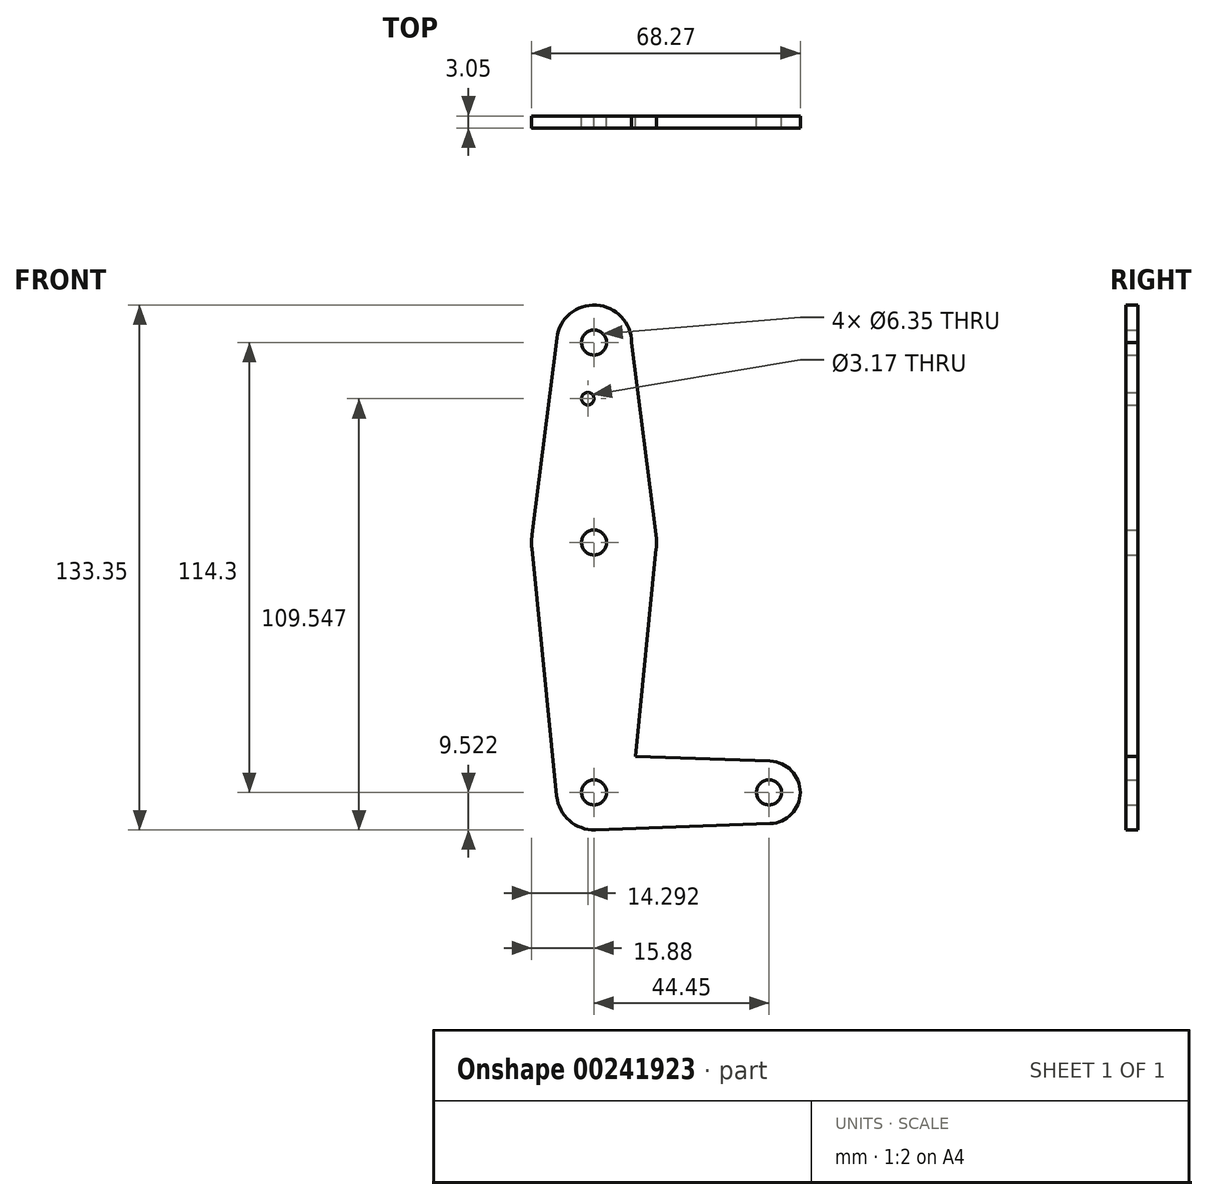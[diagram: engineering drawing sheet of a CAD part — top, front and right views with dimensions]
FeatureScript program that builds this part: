
annotation { "Feature Type Name" : "Feature", "Feature Type Description" : "" }
export const myFeature = defineFeature(function(context is Context, id is Id, definition is map)
    precondition{}
    {
        {
            var Q0;
            Q0=qCreatedBy(makeId("Front.planeOp"),FACE);
            var sketch = newSketch(context, id + "F0", { "sketchPlane" : qUnion([Q0])});
            skCircle(sketch, "E0", {"center": v(-0.34, 88.77) * mm, "radius": 9.53 * mm});
            skCircle(sketch, "E1", {"center": v(-0.34, 37.97) * mm, "radius": 15.88 * mm});
            skCircle(sketch, "E2", {"center": v(-0.34, -25.53) * mm, "radius": 9.53 * mm});
            skLineSegment(sketch, "E3", {"start": v(-0.34, 88.77) * mm, "end": v(-0.34, -25.53) * mm, "construction": true});
            skLineSegment(sketch, "E4", {"start": v(9.18, 88.77) * mm, "end": v(15.4, 39.98) * mm});
            skLineSegment(sketch, "E5", {"start": v(-9.8, 89.96) * mm, "end": v(-16.1, 39.96) * mm});
            skLineSegment(sketch, "E6", {"start": v(-9.82, -26.48) * mm, "end": v(-16.14, 36.38) * mm});
            skLineSegment(sketch, "E7", {"start": v(9.14, -26.48) * mm, "end": v(15.46, 36.38) * mm});
            skLineSegment(sketch, "E8", {"start": v(-0.34, -25.53) * mm, "end": v(44.1, -25.53) * mm, "construction": true});
            skCircle(sketch, "E9", {"center": v(44.1, -25.53) * mm, "radius": 7.94 * mm});
            skLineSegment(sketch, "E10", {"start": v(0, -16) * mm, "end": v(44.4, -17.6) * mm});
            skLineSegment(sketch, "E11", {"start": v(0, -35.05) * mm, "end": v(44.4, -33.46) * mm});
            skCircle(sketch, "E12", {"center": v(-0.34, 88.77) * mm, "radius": 3.18 * mm});
            skCircle(sketch, "E13", {"center": v(-0.34, 37.97) * mm, "radius": 3.17 * mm});
            skCircle(sketch, "E14", {"center": v(-0.34, -25.53) * mm, "radius": 3.18 * mm});
            skCircle(sketch, "E15", {"center": v(44.1, -25.53) * mm, "radius": 3.18 * mm});
            skCircle(sketch, "E16", {"center": v(-1.93, 74.5) * mm, "radius": 1.59 * mm});
            skSolve(sketch);
        }
        {
            var Q0;
            Q0 = qSketchRegion(id + "F0", true);
            extrude(context, id + "F1", {"entities" : qUnion([Q0]), "depth" : 3.05 * mm});
        }
    });
